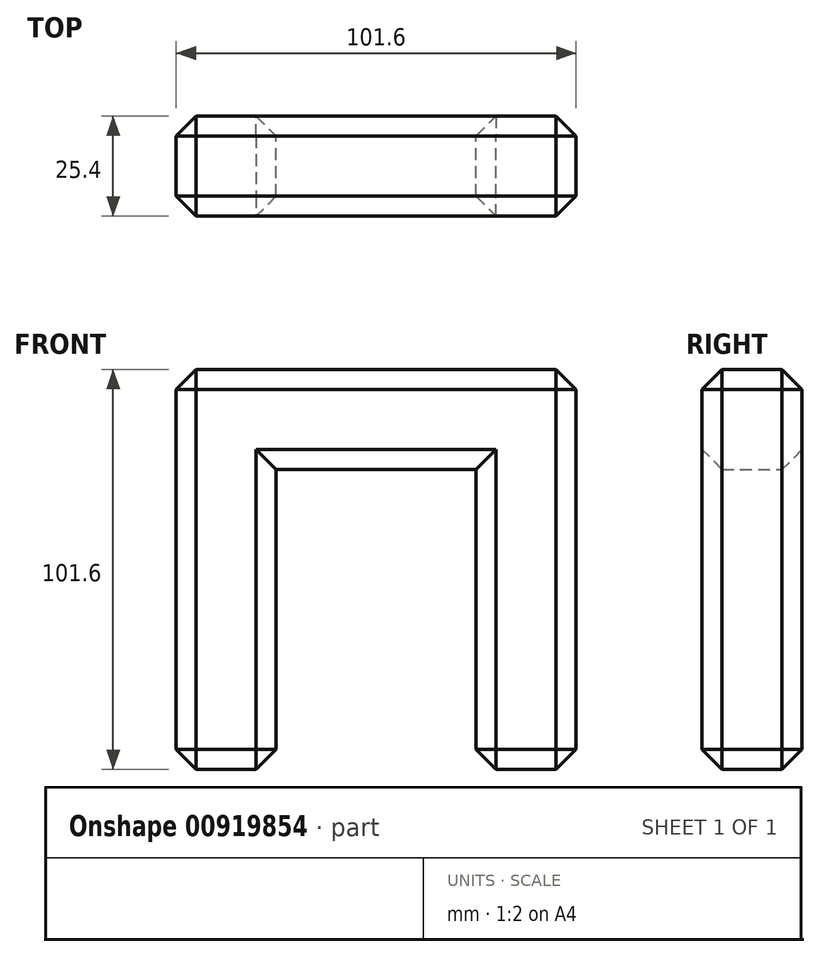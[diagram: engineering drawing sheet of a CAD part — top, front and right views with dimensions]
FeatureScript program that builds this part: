
annotation { "Feature Type Name" : "Feature", "Feature Type Description" : "" }
export const myFeature = defineFeature(function(context is Context, id is Id, definition is map)
    precondition{}
    {
        {
            var Q0;
            Q0=qCreatedBy(makeId("Front.planeOp"),FACE);
            var sketch = newSketch(context, id + "F0", { "sketchPlane" : qUnion([Q0])});
            skLineSegment(sketch, "E0", {"start": v(-50.66, 52.44) * mm, "end": v(50.94, 52.44) * mm});
            skLineSegment(sketch, "E1", {"start": v(50.94, 52.44) * mm, "end": v(50.94, -49.16) * mm});
            skLineSegment(sketch, "E2", {"start": v(50.94, -49.16) * mm, "end": v(25.54, -49.16) * mm});
            skLineSegment(sketch, "E3", {"start": v(25.54, -49.16) * mm, "end": v(25.54, 27.04) * mm});
            skLineSegment(sketch, "E4", {"start": v(25.54, 27.04) * mm, "end": v(-25.26, 27.04) * mm});
            skLineSegment(sketch, "E5", {"start": v(-25.26, 27.04) * mm, "end": v(-25.26, -49.16) * mm});
            skLineSegment(sketch, "E6", {"start": v(-25.26, -49.16) * mm, "end": v(-50.66, -49.16) * mm});
            skLineSegment(sketch, "E7", {"start": v(-50.66, -49.16) * mm, "end": v(-50.66, 52.44) * mm});
            skLineSegment(sketch, "E8", {"start": v(0, -62.72) * mm, "end": v(0, 81.4) * mm, "construction": true});
            skSolve(sketch);
        }
        {
            var Q0;
            Q0=makeQuery(id+"F0.imprint","IMPRINT",FACE,{"disambiguationData":[TD([[makeQuery(id+"F0.imprint","IMPRINT",EDGE,{"derivedFrom":sQuery(id+"F0.wireOp",EDGE,"E0")}),-1.0]])]});
            extrude(context, id + "F1", {"entities" : qUnion([Q0]), "endBound" : BoundingType.SYMMETRIC, "depth" : 25.4 * mm, "offsetDistance" : 25.4 * mm});
        }
        {
            var Q0;
            Q0=makeQuery(id+"F1.opExtrude","CAP_FACE",FACE,{"disambiguationData":[OSD([sQuery(id+"F0.wireOp",EDGE,"E0"),sQuery(id+"F0.wireOp",EDGE,"E1"),sQuery(id+"F0.wireOp",EDGE,"E2"),sQuery(id+"F0.wireOp",EDGE,"E3"),sQuery(id+"F0.wireOp",EDGE,"E4"),sQuery(id+"F0.wireOp",EDGE,"E5"),sQuery(id+"F0.wireOp",EDGE,"E6"),sQuery(id+"F0.wireOp",EDGE,"E7")])],"isStart":true});
            var Q1;
            Q1=makeQuery(id+"F1.opExtrude","CAP_FACE",FACE,{"disambiguationData":[OSD([sQuery(id+"F0.wireOp",EDGE,"E0"),sQuery(id+"F0.wireOp",EDGE,"E1"),sQuery(id+"F0.wireOp",EDGE,"E2"),sQuery(id+"F0.wireOp",EDGE,"E3"),sQuery(id+"F0.wireOp",EDGE,"E4"),sQuery(id+"F0.wireOp",EDGE,"E5"),sQuery(id+"F0.wireOp",EDGE,"E6"),sQuery(id+"F0.wireOp",EDGE,"E7")])],"isStart":false});
            var Q2;
            Q2=makeQuery(id+"F1.opExtrude","SWEPT_FACE",FACE,{"disambiguationData":[OSD([sQuery(id+"F0.wireOp",EDGE,"E0")])]});
            var Q3;
            Q3=makeQuery(id+"F1.opExtrude","SWEPT_FACE",FACE,{"disambiguationData":[OSD([sQuery(id+"F0.wireOp",EDGE,"E2")])]});
            var Q4;
            Q4=makeQuery(id+"F1.opExtrude","SWEPT_FACE",FACE,{"disambiguationData":[OSD([sQuery(id+"F0.wireOp",EDGE,"E6")])]});
            chamfer(context, id + "F2", {"entities" : qUnion([Q0, Q1, Q2, Q3, Q4]), "width" : 5.08 * mm, "tangentPropagation" : true});
        }
    });
